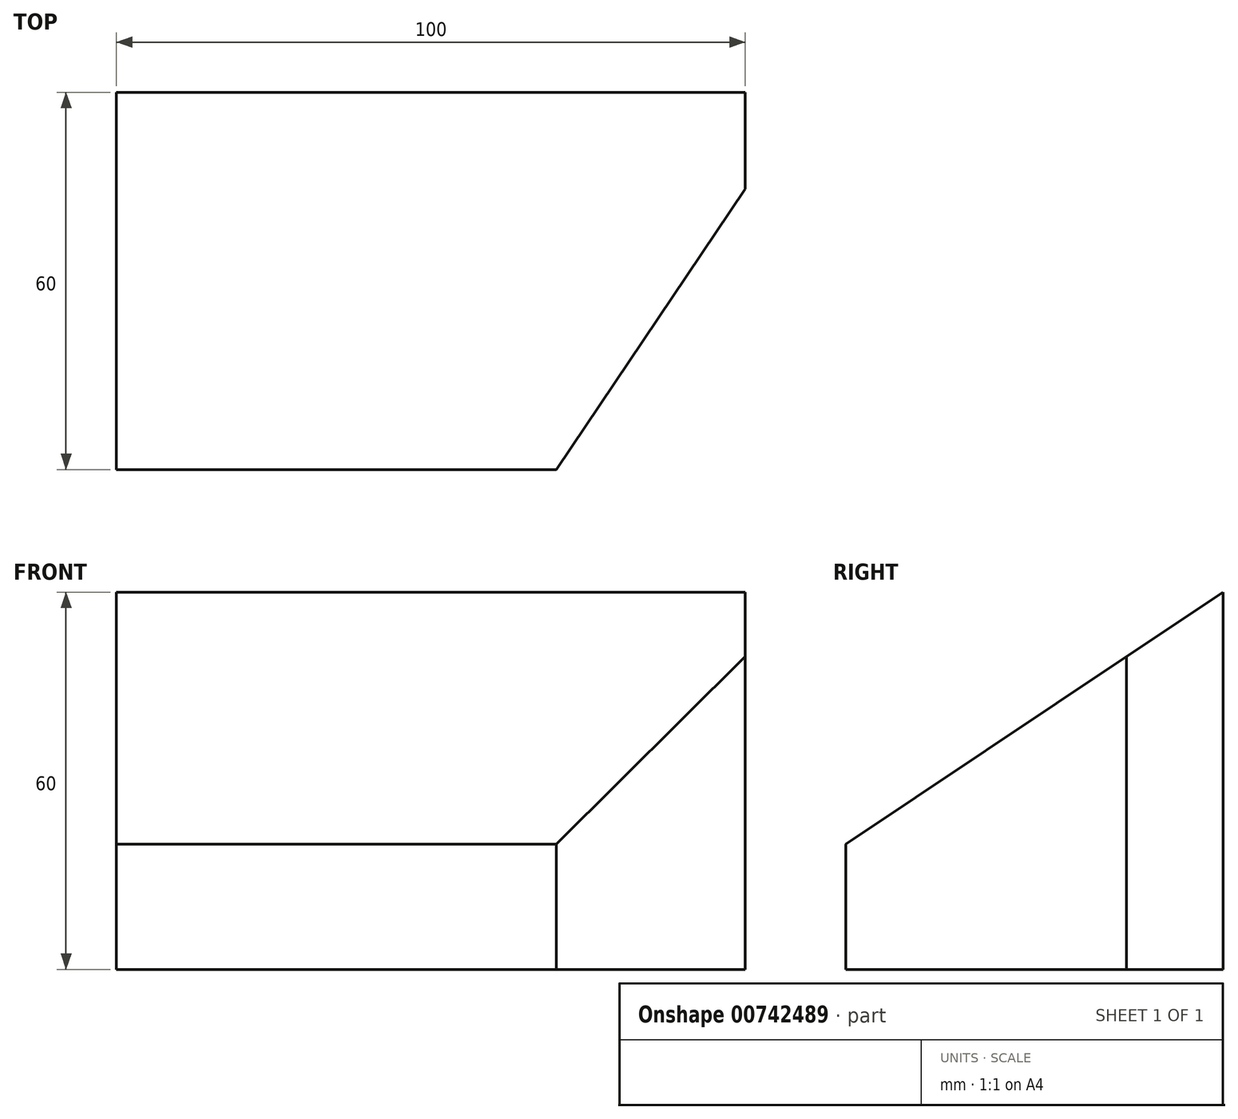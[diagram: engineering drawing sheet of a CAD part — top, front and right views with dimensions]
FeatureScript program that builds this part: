
annotation { "Feature Type Name" : "Feature", "Feature Type Description" : "" }
export const myFeature = defineFeature(function(context is Context, id is Id, definition is map)
    precondition{}
    {
        {
            var Q0;
            Q0=qCreatedBy(makeId("Front.planeOp"),FACE);
            var sketch = newSketch(context, id + "F0", { "sketchPlane" : qUnion([Q0])});
            skLineSegment(sketch, "E0.bottom", {"start": v(0, 0) * mm, "end": v(100, 0) * mm});
            skLineSegment(sketch, "E0.top", {"start": v(0, 60) * mm, "end": v(100, 60) * mm});
            skLineSegment(sketch, "E0.left", {"start": v(0, 0) * mm, "end": v(0, 60) * mm});
            skLineSegment(sketch, "E0.right", {"start": v(100, 0) * mm, "end": v(100, 60) * mm});
            skSolve(sketch);
        }
        {
            var Q0;
            Q0 = qSketchRegion(id + "F0", true);
            var Q1;
            Q1=makeQuery(id+"F0.imprint","IMPRINT",FACE,{"disambiguationData":[TD([[makeQuery(id+"F0.imprint","IMPRINT",EDGE,{"derivedFrom":sQuery(id+"F0.wireOp",EDGE,"E0.bottom")}),1.0]])]});
            extrude(context, id + "F1", {"entities" : qUnion([Q0, Q1]), "depth" : 60 * mm, "offsetDistance" : 25 * mm});
        }
        {
            var Q0;
            Q0=makeQuery(id+"F1.opExtrude","SWEPT_FACE",FACE,{"disambiguationData":[OSD([sQuery(id+"F0.wireOp",EDGE,"E0.left")])]});
            var sketch = newSketch(context, id + "F2", { "sketchPlane" : qUnion([Q0])});
            skLineSegment(sketch, "E1", {"start": v(60, 19.93) * mm, "end": v(0, 60) * mm});
            skSolve(sketch);
        }
        {
            var Q0;
            {var subQ0=sQuery(id+"F2.wireOp",EDGE,"E1");Q0=makeQuery(id+"F2.imprint","IMPRINT",FACE,{"disambiguationData":[TD([[makeQuery(id+"F2.imprint","IMPRINT",EDGE,{"derivedFrom":subQ0}),-1.0]])]});}
            extrude(context, id + "F3", {"entities" : qUnion([Q0]), "operationType" : NewBodyOperationType.REMOVE, "oppositeDirection" : true, "depth" : 100 * mm, "offsetDistance" : 25 * mm});
        }
        {
            var Q0;
            Q0=makeQuery(id+"F1.opExtrude","SWEPT_FACE",FACE,{"disambiguationData":[OSD([sQuery(id+"F0.wireOp",EDGE,"E0.bottom")])]});
            var sketch = newSketch(context, id + "F4", { "sketchPlane" : qUnion([Q0])});
            skLineSegment(sketch, "E2", {"start": v(69.93, 60) * mm, "end": v(100, 15.35) * mm});
            skSolve(sketch);
        }
        {
            var Q0;
            {var subQ0=sQuery(id+"F4.wireOp",EDGE,"E2");Q0=makeQuery(id+"F4.imprint","IMPRINT",FACE,{"disambiguationData":[TD([[makeQuery(id+"F4.imprint","IMPRINT",EDGE,{"derivedFrom":subQ0}),1.0]])]});}
            extrude(context, id + "F5", {"entities" : qUnion([Q0]), "operationType" : NewBodyOperationType.REMOVE, "oppositeDirection" : true, "depth" : 73.8 * mm, "offsetDistance" : 25 * mm});
        }
    });
